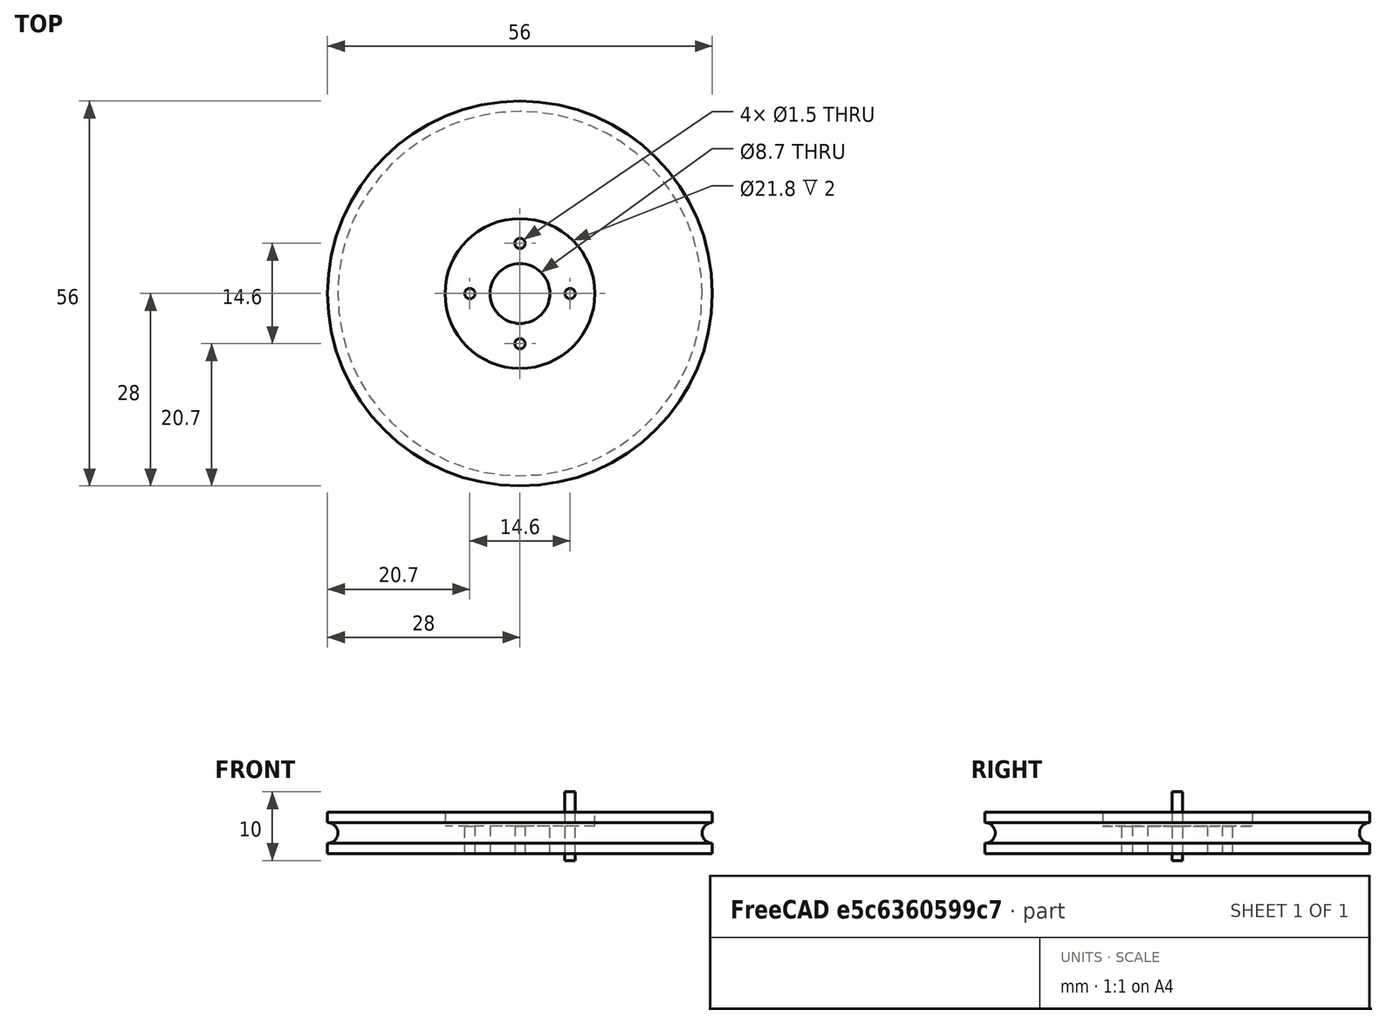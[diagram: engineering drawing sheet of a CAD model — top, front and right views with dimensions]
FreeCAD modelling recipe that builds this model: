
FCSTD DOCUMENT  (FreeCAD 0.21R33694 (Git))
Label: OJT1_T15R01_rueda
License: All rights reserved
LicenseURL: http://en.wikipedia.org/wiki/All_rights_reserved
objects: Part::Cylinder×4, Part::Cut×4, Part::Torus×1, Part::FeaturePython×1
note: 9 computed .brp shape members not serialized (recipe doc carries the construction recipe); baked Part::Feature solids carry a one-line shape summary decoded from their .brp

FEATURE [Part::Cylinder] Cylinder
  Angle = 360
  AttacherType = Attacher::AttachEngine3D
  FirstAngle = 0
  Height = 6
  Radius = 28
  SecondAngle = 0
FEATURE [Part::Torus] Torus001
  Angle1 = -180
  Angle2 = 180
  Angle3 = 360
  AttacherType = Attacher::AttachEngine3D
  Placement = pos=(0,0,3) rot=(0,0,1;0rad)
  Radius1 = 28
  Radius2 = 1.5
FEATURE [Part::Cut] Cut
  Base = -> Cylinder
  Refine = true
  Tool = -> Torus001
FEATURE [Part::Cylinder] Cylinder001
  Angle = 360
  AttacherType = Attacher::AttachEngine3D
  FirstAngle = 0
  Height = 10
  Placement = pos=(0,0,4) rot=(0,0,1;0rad)
  Radius = 10.9
  SecondAngle = 0
FEATURE [Part::Cut] Cut001
  Base = -> Cut
  Refine = true
  Tool = -> Cylinder001
FEATURE [Part::Cylinder] Cylinder002
  Angle = 360
  AttacherType = Attacher::AttachEngine3D
  FirstAngle = 0
  Height = 10
  Placement = pos=(0,0,-1) rot=(0,0,1;0rad)
  Radius = 4.35
  SecondAngle = 0
FEATURE [Part::Cut] Cut002
  Base = -> Cut001
  Refine = true
  Tool = -> Cylinder002
FEATURE [Part::Cylinder] Cylinder003
  Angle = 360
  AttacherType = Attacher::AttachEngine3D
  FirstAngle = 0
  Height = 10
  Placement = pos=(7.3,0,-1) rot=(0,0,1;0rad)
  Radius = 0.75
  SecondAngle = 0
FEATURE [Part::FeaturePython] Array  # Draft array (typed FeaturePython)
  AlwaysSyncPlacement = false
  Angle = 360
  ArrayType = 1
  Axis = (0,0,1)
  Base = -> Cylinder003
  Center = (0,0,0)
  Count = 4
  ExpandArray = false
  Fuse = false
  IntervalAxis = (0,0,0)
  IntervalX = (100,0,0)
  IntervalY = (0,100,0)
  IntervalZ = (0,0,100)
  NumberCircles = 3
  NumberPolar = 4
  NumberX = 2
  NumberY = 2
  NumberZ = 1
  PlacementList = 4 placements: [(7.3,0,-1),(0,7.3,-1),(-7.3,8.93992e-16,-1),(-1.62093e-15,-7.3,-1)]
  RadialDistance = 50
  ScaleList = (4) [(1,1,1),(1,1,1),(1,1,1),(1,1,1)]
  Symmetry = 1
  TangentialDistance = 25
FEATURE [Part::Cut] Cut003
  Base = -> Cut002
  Refine = true
  Tool = -> Array
